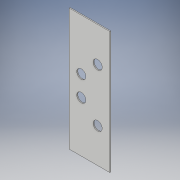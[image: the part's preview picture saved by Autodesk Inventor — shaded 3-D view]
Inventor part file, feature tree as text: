
AUTODESK INVENTOR PART (.ipt)
format: ipt  version: 2018 (Build 220112000, 112)  size: 122,368 bytes
history: native  units: in
note: dims shown in document units (in); Inventor stores cm internally (conversion verified against a paired STEP export)
features: extrude x2, sketch x2
ambient origin geometry x8: Origin, YZ Plane, XZ Plane, XY Plane, X Axis, Y Axis, Z Axis, Center Point
bodies: Solid1 (feature_tree)
feature tree (4):
  extrude  "Extrusion1"  Depth=15.0in
  extrude  "Extrusion2"  Depth=0.125in
  sketch  "Sketch1"  dims[d0=5.0in d1=15.0in]
  sketch  "Sketch3"  dims[d2=0.125in d3=0.0in d20=0.25in d21=1.25in d22=1.25in d23=90.0deg d24=1.25in d25=90.0deg d26=2.0in d27=2.0in d28=1.125in d29=2.0in d30=2.0in d31=1.125in d34=1.0in d35=0.0in d36=1.125in d37=1.125in]
